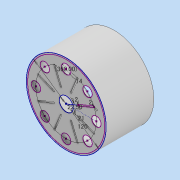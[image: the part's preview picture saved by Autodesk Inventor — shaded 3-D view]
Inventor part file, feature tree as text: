
AUTODESK INVENTOR PART (.ipt)
format: ipt  version: 2022 (Build 260153000, 153)  size: 251,904 bytes
history: native  units: mm
features: extrude x3, other x2, fillet x2, pattern_circular x1
ambient origin geometry x8: Origin, YZ Plane, XZ Plane, XY Plane, X Axis, Y Axis, Z Axis, Center Point
bodies: Body1 (feature_tree)
feature tree (8):
  other  "ソリッド1"
  other  "BASEsc"
  extrude  "押し出し1"  Depth=120.0mm
  extrude  "押し出し2"  Depth=21.0mm
  fillet  "フィレット1"  Radius=14.0mm
  extrude  "押し出し3"  Depth=80.0mm TaperAngle=360.0deg
  pattern_circular  "円形状パターン1"  [2 undecoded]
  fillet  "フィレット2"  Radius=72.0mm
note: 2 required parameter values undecoded (feature->parameter linkage not recoverable at this tier; creation-order binding heuristic only, values carry confidence <= 0.55)
